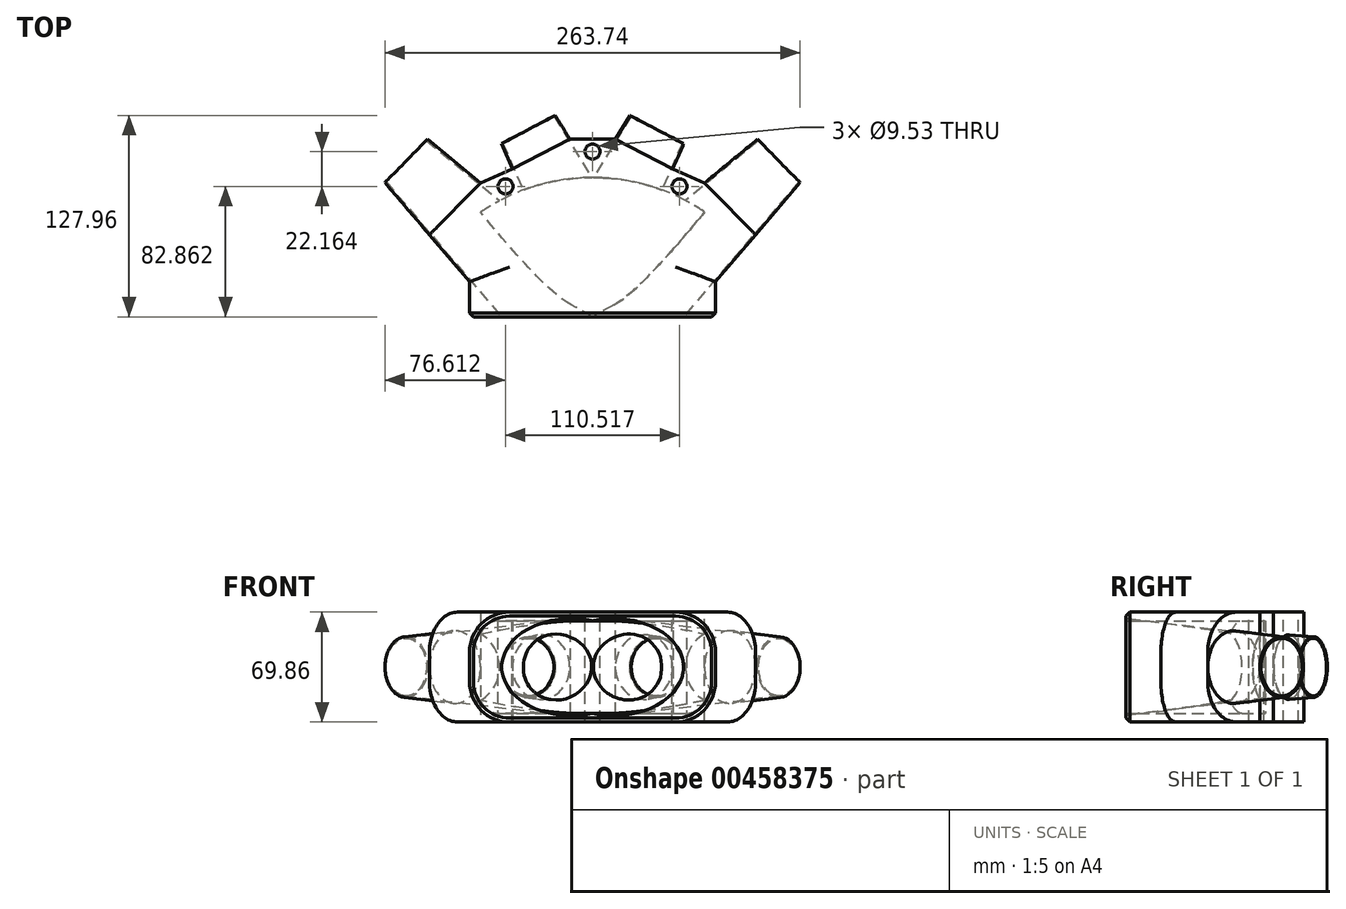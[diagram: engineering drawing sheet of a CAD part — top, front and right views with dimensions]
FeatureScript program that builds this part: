
annotation { "Feature Type Name" : "Feature", "Feature Type Description" : "" }
export const myFeature = defineFeature(function(context is Context, id is Id, definition is map)
    precondition{}
    {
        {
            var Q0;
            Q0=qCreatedBy(makeId("Top.planeOp"),FACE);
            var sketch = newSketch(context, id + "F0", { "sketchPlane" : qUnion([Q0])});
            skLineSegment(sketch, "E0", {"start": v(78.1, 11.18) * mm, "end": v(131.87, 74.09) * mm});
            skLineSegment(sketch, "E1", {"start": v(131.87, 74.09) * mm, "end": v(101.6, 11.18) * mm});
            skLineSegment(sketch, "E2", {"start": v(-5.07, 11.18) * mm, "end": v(104.82, 101.64) * mm});
            skLineSegment(sketch, "E3", {"start": v(104.82, 101.64) * mm, "end": v(101.6, 11.18) * mm});
            skLineSegment(sketch, "E4", {"start": v(19.9, 11.18) * mm, "end": v(57.9, 98.84) * mm});
            skLineSegment(sketch, "E5", {"start": v(57.9, 98.84) * mm, "end": v(101.6, 11.18) * mm});
            skLineSegment(sketch, "E6", {"start": v(-42.1, 11.18) * mm, "end": v(23.72, 116.78) * mm});
            skLineSegment(sketch, "E7", {"start": v(23.72, 116.78) * mm, "end": v(101.6, 11.18) * mm});
            skLineSegment(sketch, "E8", {"start": v(23.72, 116.78) * mm, "end": v(57.9, 98.84) * mm});
            skLineSegment(sketch, "E9", {"start": v(104.82, 101.64) * mm, "end": v(131.87, 74.09) * mm});
            skLineSegment(sketch, "E10.MirrorCS", {"start": v(-23.72, 116.78) * mm, "end": v(-57.9, 98.84) * mm});
            skLineSegment(sketch, "E11.MirrorCS", {"start": v(-104.82, 101.64) * mm, "end": v(-131.87, 74.09) * mm});
            skLineSegment(sketch, "E12.MirrorCS", {"start": v(42.1, 11.18) * mm, "end": v(-23.72, 116.78) * mm});
            skLineSegment(sketch, "E13.MirrorCS", {"start": v(-19.9, 11.18) * mm, "end": v(-57.9, 98.84) * mm});
            skLineSegment(sketch, "E14.MirrorCS", {"start": v(5.07, 11.18) * mm, "end": v(-104.82, 101.64) * mm});
            skLineSegment(sketch, "E15.MirrorCS", {"start": v(-78.1, 11.18) * mm, "end": v(-131.87, 74.09) * mm});
            skLineSegment(sketch, "E16", {"start": v(-78.1, 11.18) * mm, "end": v(-42.1, 11.18) * mm});
            skLineSegment(sketch, "E17", {"start": v(-42.1, 11.18) * mm, "end": v(-19.9, 11.18) * mm});
            skLineSegment(sketch, "E18", {"start": v(-19.9, 11.18) * mm, "end": v(-5.07, 11.18) * mm});
            skLineSegment(sketch, "E19", {"start": v(-5.07, 11.18) * mm, "end": v(5.07, 11.18) * mm});
            skLineSegment(sketch, "E20", {"start": v(5.07, 11.18) * mm, "end": v(19.9, 11.18) * mm});
            skLineSegment(sketch, "E21", {"start": v(19.9, 11.18) * mm, "end": v(42.1, 11.18) * mm});
            skLineSegment(sketch, "E22", {"start": v(42.1, 11.18) * mm, "end": v(78.1, 11.18) * mm});
            skSolve(sketch);
        }
        {
            var Q0;
            Q0=sQuery(id+"F0.wireOp",EDGE,"E11.MirrorCS");
            cPlane(context, id + "F1", {"entities" : qUnion([Q0]), "cplaneType" : CPlaneType.LINE_ANGLE, "offset" : 25 * mm, "angle" : 270 * degree, "width" : 150 * mm, "height" : 150 * mm});
        }
        {
            var Q0;
            Q0=sQuery(id+"F0.wireOp",EDGE,"E10.MirrorCS");
            cPlane(context, id + "F2", {"entities" : qUnion([Q0]), "cplaneType" : CPlaneType.LINE_ANGLE, "offset" : 25 * mm, "angle" : 180 * degree, "width" : 150 * mm, "height" : 150 * mm});
        }
        {
            var Q0;
            Q0=sQuery(id+"F0.wireOp",EDGE,"E8");
            cPlane(context, id + "F3", {"entities" : qUnion([Q0]), "cplaneType" : CPlaneType.LINE_ANGLE, "offset" : 25 * mm, "angle" : 0 * degree, "width" : 150 * mm, "height" : 150 * mm});
        }
        {
            var Q0;
            Q0=sQuery(id+"F0.wireOp",EDGE,"E9");
            cPlane(context, id + "F4", {"entities" : qUnion([Q0]), "cplaneType" : CPlaneType.LINE_ANGLE, "offset" : 25 * mm, "angle" : 90 * degree, "width" : 150 * mm, "height" : 150 * mm});
        }
        {
            var Q0;
            Q0=qCreatedBy(id+"F1.planeOp",FACE);
            var sketch = newSketch(context, id + "F5", { "sketchPlane" : qUnion([Q0])});
            skCircle(sketch, "E23", {"center": v(20.21, 0) * mm, "radius": 19.3 * mm});
            skCircle(sketch, "E24", {"center": v(20.21, 0) * mm, "radius": 18.35 * mm});
            skSolve(sketch);
        }
        {
            var Q0;
            Q0=qCreatedBy(id+"F2.planeOp",FACE);
            var sketch = newSketch(context, id + "F6", { "sketchPlane" : qUnion([Q0])});
            skCircle(sketch, "E25", {"center": v(-13.96, 0) * mm, "radius": 19.3 * mm});
            skCircle(sketch, "E26", {"center": v(-13.96, 0) * mm, "radius": 18.35 * mm});
            skSolve(sketch);
        }
        {
            var Q0;
            Q0=qCreatedBy(id+"F3.planeOp",FACE);
            var sketch = newSketch(context, id + "F7", { "sketchPlane" : qUnion([Q0])});
            skCircle(sketch, "E27", {"center": v(13.96, 0) * mm, "radius": 19.3 * mm});
            skCircle(sketch, "E28", {"center": v(13.96, 0) * mm, "radius": 18.35 * mm});
            skSolve(sketch);
        }
        {
            var Q0;
            Q0=qCreatedBy(id+"F4.planeOp",FACE);
            var sketch = newSketch(context, id + "F8", { "sketchPlane" : qUnion([Q0])});
            skCircle(sketch, "E29", {"center": v(-20.21, 0) * mm, "radius": 19.3 * mm});
            skCircle(sketch, "E30", {"center": v(-20.21, 0) * mm, "radius": 18.35 * mm});
            skSolve(sketch);
        }
        {
            var Q0;
            Q0=qCreatedBy(makeId("Top.planeOp"),FACE);
            var sketch = newSketch(context, id + "F9", { "sketchPlane" : qUnion([Q0])});
            skLineSegment(sketch, "E31", {"start": v(-78.1, 11.18) * mm, "end": v(78.1, 11.18) * mm});
            skLineSegment(sketch, "E32.bottom", {"start": v(-78.1, 11.18) * mm, "end": v(101.6, 11.18) * mm});
            skLineSegment(sketch, "E32.top", {"start": v(-78.1, -11.18) * mm, "end": v(78.1, -11.18) * mm});
            skLineSegment(sketch, "E32.left", {"start": v(-78.1, 11.18) * mm, "end": v(-78.1, -11.18) * mm});
            skLineSegment(sketch, "E32.right", {"start": v(78.1, 11.18) * mm, "end": v(78.1, -11.18) * mm});
            skCircle(sketch, "E33", {"center": v(-55.26, 71.68) * mm, "radius": 8.37 * mm});
            skCircle(sketch, "E34", {"center": v(0, 93.85) * mm, "radius": 8 * mm});
            skCircle(sketch, "E35", {"center": v(55.26, 71.68) * mm, "radius": 8.37 * mm});
            skLineSegment(sketch, "E36", {"start": v(-14.41, 101.85) * mm, "end": v(14.41, 101.85) * mm});
            skLineSegment(sketch, "E37", {"start": v(-71.15, 73.92) * mm, "end": v(-50.9, 82.7) * mm});
            skLineSegment(sketch, "E38", {"start": v(50.9, 82.7) * mm, "end": v(71.15, 73.92) * mm});
            skLineSegment(sketch, "E39", {"start": v(-78.1, 11.18) * mm, "end": v(-59, -11.18) * mm});
            skLineSegment(sketch, "E40", {"start": v(78.1, 11.18) * mm, "end": v(59, -11.18) * mm});
            skLineSegment(sketch, "E41", {"start": v(-50.9, 82.7) * mm, "end": v(-57.9, 98.84) * mm});
            skLineSegment(sketch, "E42", {"start": v(-57.9, 98.84) * mm, "end": v(-23.72, 116.78) * mm});
            skLineSegment(sketch, "E43", {"start": v(-23.72, 116.78) * mm, "end": v(-14.41, 101.85) * mm});
            skLineSegment(sketch, "E44", {"start": v(14.41, 101.85) * mm, "end": v(23.72, 116.78) * mm});
            skLineSegment(sketch, "E45", {"start": v(23.72, 116.78) * mm, "end": v(57.9, 98.84) * mm});
            skLineSegment(sketch, "E46", {"start": v(57.9, 98.84) * mm, "end": v(50.9, 82.7) * mm});
            skLineSegment(sketch, "E47", {"start": v(71.15, 73.92) * mm, "end": v(104.82, 101.64) * mm});
            skLineSegment(sketch, "E48", {"start": v(104.82, 101.64) * mm, "end": v(131.87, 74.09) * mm});
            skLineSegment(sketch, "E49", {"start": v(131.87, 74.09) * mm, "end": v(78.1, 11.18) * mm});
            skLineSegment(sketch, "E50", {"start": v(-71.15, 73.92) * mm, "end": v(-104.82, 101.64) * mm});
            skLineSegment(sketch, "E51", {"start": v(-104.82, 101.64) * mm, "end": v(-131.87, 74.09) * mm});
            skLineSegment(sketch, "E52", {"start": v(-131.87, 74.09) * mm, "end": v(-78.1, 11.18) * mm});
            skSolve(sketch);
        }
        {
            var Q0;
            Q0=makeQuery(id+"F9.imprint","IMPRINT",FACE,{"disambiguationData":[TD([[makeQuery(id+"F9.imprint","IMPRINT",EDGE,{"derivedFrom":sQuery(id+"F9.wireOp",EDGE,"E33")}),1.0]])]});
            var Q1;
            Q1=makeQuery(id+"F9.imprint","IMPRINT",FACE,{"disambiguationData":[TD([[makeQuery(id+"F9.imprint","IMPRINT",EDGE,{"derivedFrom":sQuery(id+"F9.wireOp",EDGE,"E34")}),1.0]])]});
            var Q2;
            Q2=makeQuery(id+"F9.imprint","IMPRINT",FACE,{"disambiguationData":[TD([[makeQuery(id+"F9.imprint","IMPRINT",EDGE,{"derivedFrom":sQuery(id+"F9.wireOp",EDGE,"E35")}),1.0]])]});
            var Q3;
            {var subQ0=sQuery(id+"F9.wireOp",EDGE,"E39");Q3=makeQuery(id+"F9.imprint","IMPRINT",FACE,{"disambiguationData":[TD([[makeQuery(id+"F9.imprint","IMPRINT",EDGE,{"derivedFrom":subQ0}),1.0]])]});}
            var Q4;
            {var subQ7=sQuery(id+"F9.wireOp",EDGE,"E33");Q4=makeQuery(id+"F9.imprint","IMPRINT",FACE,{"disambiguationData":[TD([[makeQuery(id+"F9.imprint","IMPRINT",EDGE,{"derivedFrom":subQ7}),-1.0]])]});}
            var Q5;
            {var subQ0=sQuery(id+"F9.wireOp",EDGE,"E32.left");Q5=makeQuery(id+"F9.imprint","IMPRINT",FACE,{"disambiguationData":[TD([[makeQuery(id+"F9.imprint","IMPRINT",EDGE,{"derivedFrom":subQ0}),1.0]])]});}
            var Q6;
            {var subQ0=sQuery(id+"F9.wireOp",EDGE,"E32.right");Q6=makeQuery(id+"F9.imprint","IMPRINT",FACE,{"disambiguationData":[TD([[makeQuery(id+"F9.imprint","IMPRINT",EDGE,{"derivedFrom":subQ0}),-1.0]])]});}
            extrude(context, id + "F10", {"entities" : qUnion([Q0, Q1, Q2, Q3, Q4, Q5, Q6]), "endBound" : BoundingType.SYMMETRIC, "depth" : 69.85 * mm});
        }
        {
            var Q0;
            Q0=qCreatedBy(makeId("Top.planeOp"),FACE);
            var sketch = newSketch(context, id + "F11", { "sketchPlane" : qUnion([Q0])});
            skLineSegment(sketch, "E53", {"start": v(118.35, 87.86) * mm, "end": v(0, -28.32) * mm});
            skLineSegment(sketch, "E54", {"start": v(0, -28.32) * mm, "end": v(-118.35, 87.86) * mm});
            skSolve(sketch);
        }
        {
            var Q0;
            Q0=makeQuery(id+"F10.opExtrude","SWEPT_FACE",FACE,{"disambiguationData":[OSD([sQuery(id+"F9.wireOp",EDGE,"E51")])]});
            var Q1;
            Q1=makeQuery(id+"F10.opExtrude","CAP_VERTEX",VERTEX,{"disambiguationData":[OSD([sQuery(id+"F9.wireOp",EDGE,"E37"),sQuery(id+"F9.wireOp",EDGE,"E50")])],"isStart":true});
            extrude(context, id + "F12", {"entities" : qUnion([Q0]), "operationType" : NewBodyOperationType.REMOVE, "endBound" : BoundingType.UP_TO_VERTEX, "oppositeDirection" : true, "endBoundEntityVertex" : qUnion([Q1]), "depth" : 25 * mm, "hasDraft" : true, "draftAngle" : 5 * degree});
        }
        {
            var Q0;
            Q0=makeQuery(id+"F10.opExtrude","SWEPT_FACE",FACE,{"disambiguationData":[OSD([sQuery(id+"F9.wireOp",EDGE,"E42")])]});
            var Q1;
            Q1=makeQuery(id+"F10.opExtrude","CAP_VERTEX",VERTEX,{"disambiguationData":[OSD([sQuery(id+"F9.wireOp",EDGE,"E36"),sQuery(id+"F9.wireOp",EDGE,"E43")])],"isStart":false});
            extrude(context, id + "F13", {"entities" : qUnion([Q0]), "operationType" : NewBodyOperationType.REMOVE, "endBound" : BoundingType.UP_TO_VERTEX, "oppositeDirection" : true, "endBoundEntityVertex" : qUnion([Q1]), "depth" : 25 * mm, "hasDraft" : true, "draftAngle" : 5 * degree});
        }
        {
            var Q0;
            Q0=makeQuery(id+"F10.opExtrude","SWEPT_FACE",FACE,{"disambiguationData":[OSD([sQuery(id+"F9.wireOp",EDGE,"E45")])]});
            var Q1;
            Q1=makeQuery(id+"F10.opExtrude","CAP_VERTEX",VERTEX,{"disambiguationData":[OSD([sQuery(id+"F9.wireOp",EDGE,"E36"),sQuery(id+"F9.wireOp",EDGE,"E44")])],"isStart":false});
            extrude(context, id + "F14", {"entities" : qUnion([Q0]), "operationType" : NewBodyOperationType.REMOVE, "endBound" : BoundingType.UP_TO_VERTEX, "oppositeDirection" : true, "endBoundEntityVertex" : qUnion([Q1]), "depth" : 25 * mm, "hasDraft" : true, "draftAngle" : 5 * degree});
        }
        {
            var Q0;
            Q0=makeQuery(id+"F10.opExtrude","SWEPT_FACE",FACE,{"disambiguationData":[OSD([sQuery(id+"F9.wireOp",EDGE,"E48")])]});
            var Q1;
            Q1=makeQuery(id+"F10.opExtrude","CAP_VERTEX",VERTEX,{"disambiguationData":[OSD([sQuery(id+"F9.wireOp",EDGE,"E38"),sQuery(id+"F9.wireOp",EDGE,"E47")])],"isStart":false});
            extrude(context, id + "F15", {"entities" : qUnion([Q0]), "operationType" : NewBodyOperationType.REMOVE, "endBound" : BoundingType.UP_TO_VERTEX, "oppositeDirection" : true, "endBoundEntityVertex" : qUnion([Q1]), "depth" : 25 * mm, "hasDraft" : true, "draftAngle" : 5 * degree});
        }
        {
            var Q0;
            Q0=makeQuery(id+"F6.imprint","IMPRINT",FACE,{"disambiguationData":[TD([[makeQuery(id+"F6.imprint","IMPRINT",EDGE,{"derivedFrom":sQuery(id+"F6.wireOp",EDGE,"E25")}),1.0]])]});
            var Q1;
            Q1=makeQuery(id+"F6.imprint","IMPRINT",FACE,{"disambiguationData":[TD([[makeQuery(id+"F6.imprint","IMPRINT",EDGE,{"derivedFrom":sQuery(id+"F6.wireOp",EDGE,"E26")}),1.0]])]});
            extrude(context, id + "F16", {"entities" : qUnion([Q0, Q1]), "operationType" : NewBodyOperationType.ADD, "endBound" : BoundingType.UP_TO_NEXT, "oppositeDirection" : true, "depth" : 25 * mm, "hasDraft" : true, "draftAngle" : 4 * degree});
        }
        {
            var Q0;
            Q0=makeQuery(id+"F7.imprint","IMPRINT",FACE,{"disambiguationData":[TD([[makeQuery(id+"F7.imprint","IMPRINT",EDGE,{"derivedFrom":sQuery(id+"F7.wireOp",EDGE,"E27")}),1.0]])]});
            var Q1;
            Q1=makeQuery(id+"F7.imprint","IMPRINT",FACE,{"disambiguationData":[TD([[makeQuery(id+"F7.imprint","IMPRINT",EDGE,{"derivedFrom":sQuery(id+"F7.wireOp",EDGE,"E28")}),1.0]])]});
            extrude(context, id + "F17", {"entities" : qUnion([Q0, Q1]), "operationType" : NewBodyOperationType.ADD, "endBound" : BoundingType.UP_TO_NEXT, "oppositeDirection" : true, "depth" : 25 * mm, "hasDraft" : true, "draftAngle" : 4 * degree});
        }
        {
            var Q0;
            Q0=makeQuery(id+"F8.imprint","IMPRINT",FACE,{"disambiguationData":[TD([[makeQuery(id+"F8.imprint","IMPRINT",EDGE,{"derivedFrom":sQuery(id+"F8.wireOp",EDGE,"E29")}),1.0]])]});
            var Q1;
            Q1=makeQuery(id+"F8.imprint","IMPRINT",FACE,{"disambiguationData":[TD([[makeQuery(id+"F8.imprint","IMPRINT",EDGE,{"derivedFrom":sQuery(id+"F8.wireOp",EDGE,"E30")}),1.0]])]});
            extrude(context, id + "F18", {"entities" : qUnion([Q0, Q1]), "operationType" : NewBodyOperationType.ADD, "endBound" : BoundingType.UP_TO_NEXT, "oppositeDirection" : true, "depth" : 25 * mm, "hasDraft" : true, "draftAngle" : 5 * degree});
        }
        {
            var Q0;
            Q0=makeQuery(id+"F5.imprint","IMPRINT",FACE,{"disambiguationData":[TD([[makeQuery(id+"F5.imprint","IMPRINT",EDGE,{"derivedFrom":sQuery(id+"F5.wireOp",EDGE,"E23")}),1.0]])]});
            var Q1;
            Q1=makeQuery(id+"F5.imprint","IMPRINT",FACE,{"disambiguationData":[TD([[makeQuery(id+"F5.imprint","IMPRINT",EDGE,{"derivedFrom":sQuery(id+"F5.wireOp",EDGE,"E24")}),1.0]])]});
            extrude(context, id + "F19", {"entities" : qUnion([Q0, Q1]), "operationType" : NewBodyOperationType.ADD, "endBound" : BoundingType.UP_TO_NEXT, "oppositeDirection" : true, "depth" : 25 * mm, "hasDraft" : true, "draftAngle" : 5 * degree});
        }
        {
            var Q0;
            Q0=makeQuery(id+"F5.imprint","IMPRINT",FACE,{"disambiguationData":[TD([[makeQuery(id+"F5.imprint","IMPRINT",EDGE,{"derivedFrom":sQuery(id+"F5.wireOp",EDGE,"E24")}),1.0]])]});
            extrude(context, id + "F20", {"entities" : qUnion([Q0]), "operationType" : NewBodyOperationType.REMOVE, "endBound" : BoundingType.THROUGH_ALL, "oppositeDirection" : true, "depth" : 25 * mm, "hasDraft" : true, "draftAngle" : 5 * degree});
        }
        {
            var Q0;
            Q0=makeQuery(id+"F6.imprint","IMPRINT",FACE,{"disambiguationData":[TD([[makeQuery(id+"F6.imprint","IMPRINT",EDGE,{"derivedFrom":sQuery(id+"F6.wireOp",EDGE,"E26")}),1.0]])]});
            extrude(context, id + "F21", {"entities" : qUnion([Q0]), "operationType" : NewBodyOperationType.REMOVE, "endBound" : BoundingType.THROUGH_ALL, "oppositeDirection" : true, "depth" : 25 * mm, "hasDraft" : true, "draftAngle" : 4 * degree});
        }
        {
            var Q0;
            Q0=makeQuery(id+"F7.imprint","IMPRINT",FACE,{"disambiguationData":[TD([[makeQuery(id+"F7.imprint","IMPRINT",EDGE,{"derivedFrom":sQuery(id+"F7.wireOp",EDGE,"E28")}),1.0]])]});
            extrude(context, id + "F22", {"entities" : qUnion([Q0]), "operationType" : NewBodyOperationType.REMOVE, "endBound" : BoundingType.THROUGH_ALL, "oppositeDirection" : true, "depth" : 25 * mm, "hasDraft" : true, "draftAngle" : 4 * degree});
        }
        {
            var Q0;
            Q0=makeQuery(id+"F8.imprint","IMPRINT",FACE,{"disambiguationData":[TD([[makeQuery(id+"F8.imprint","IMPRINT",EDGE,{"derivedFrom":sQuery(id+"F8.wireOp",EDGE,"E30")}),1.0]])]});
            extrude(context, id + "F23", {"entities" : qUnion([Q0]), "operationType" : NewBodyOperationType.REMOVE, "endBound" : BoundingType.THROUGH_ALL, "oppositeDirection" : true, "depth" : 25 * mm, "hasDraft" : true, "draftAngle" : 5 * degree});
        }
        {
            var Q0;
            Q0=sQuery(id+"F11.wireOp",EDGE,"E53");
            cPlane(context, id + "F24", {"entities" : qUnion([Q0]), "cplaneType" : CPlaneType.LINE_ANGLE, "offset" : 25 * mm, "angle" : 270 * degree, "width" : 150 * mm, "height" : 150 * mm});
        }
        {
            var Q0;
            Q0=qCreatedBy(id+"F24.planeOp",FACE);
            var sketch = newSketch(context, id + "F25", { "sketchPlane" : qUnion([Q0])});
            skLineSegment(sketch, "E55.bottom", {"start": v(19.84, 28.58) * mm, "end": v(-80.16, 28.57) * mm});
            skLineSegment(sketch, "E55.top", {"start": v(19.84, 0) * mm, "end": v(-80.16, 0) * mm});
            skLineSegment(sketch, "E55.left", {"start": v(19.84, 28.58) * mm, "end": v(19.84, 0) * mm});
            skLineSegment(sketch, "E55.right", {"start": v(-80.16, 28.57) * mm, "end": v(-80.16, 0) * mm});
            skLineSegment(sketch, "E56.MirrorCS", {"start": v(19.84, -28.57) * mm, "end": v(19.84, 0) * mm});
            skLineSegment(sketch, "E57.MirrorCS", {"start": v(19.84, -28.57) * mm, "end": v(-80.16, -28.57) * mm});
            skLineSegment(sketch, "E58.MirrorCS", {"start": v(-80.16, -28.57) * mm, "end": v(-80.16, 0) * mm});
            skSolve(sketch);
        }
        {
            var Q0;
            {var subQ0=sQuery(id+"F9.wireOp",EDGE,"E52");var subQ1=sQuery(id+"F9.wireOp",EDGE,"E39");Q0=makeQuery(id+"F9ZJCy9J1rFDsAn_1.boolean.opBoolean","SPLIT",EDGE,{"disambiguationData":[TD([makeQuery(id+"F12.boolean.opBoolean","COPY",FACE,{"derivedFrom":makeQuery(id+"F12.opExtrude","CAP_FACE",FACE,{"disambiguationData":[OSD([dummyQuery(id+"F12.vertexPlane.planeOp",FACE)])],"isStart":false})})])],"derivedFrom":makeQuery(id+"F10.opExtrude","CAP_EDGE",EDGE,{"disambiguationData":[OSD([subQ1,subQ0])],"isStart":false})});}
            var Q1;
            {var subQ0=sQuery(id+"F9.wireOp",EDGE,"E52");var subQ1=sQuery(id+"F9.wireOp",EDGE,"E39");Q1=makeQuery(id+"F9ZJCy9J1rFDsAn_1.boolean.opBoolean","SPLIT",EDGE,{"disambiguationData":[TD([makeQuery(id+"F12.boolean.opBoolean","COPY",FACE,{"derivedFrom":makeQuery(id+"F12.opExtrude","CAP_FACE",FACE,{"disambiguationData":[OSD([dummyQuery(id+"F12.vertexPlane.planeOp",FACE)])],"isStart":false})})])],"derivedFrom":makeQuery(id+"F10.opExtrude","CAP_EDGE",EDGE,{"disambiguationData":[OSD([subQ1,subQ0])],"isStart":true})});}
            var Q2;
            {var subQ0=sQuery(id+"F9.wireOp",EDGE,"E32.top");var subQ1=sQuery(id+"F9.wireOp",EDGE,"E52");var subQ2=sQuery(id+"F9.wireOp",EDGE,"E39");Q2=makeQuery(id+"F9ZJCy9J1rFDsAn_1.boolean.opBoolean","SPLIT",EDGE,{"disambiguationData":[TD([makeQuery(id+"F10.opExtrude","SWEPT_FACE",FACE,{"disambiguationData":[OSD([subQ0])]})])],"derivedFrom":makeQuery(id+"F10.opExtrude","CAP_EDGE",EDGE,{"disambiguationData":[OSD([subQ2,subQ1])],"isStart":false})});}
            var Q3;
            {var subQ0=sQuery(id+"F9.wireOp",EDGE,"E32.top");var subQ1=sQuery(id+"F9.wireOp",EDGE,"E52");var subQ2=sQuery(id+"F9.wireOp",EDGE,"E39");Q3=makeQuery(id+"F9ZJCy9J1rFDsAn_1.boolean.opBoolean","SPLIT",EDGE,{"disambiguationData":[TD([makeQuery(id+"F10.opExtrude","SWEPT_FACE",FACE,{"disambiguationData":[OSD([subQ0])]})])],"derivedFrom":makeQuery(id+"F10.opExtrude","CAP_EDGE",EDGE,{"disambiguationData":[OSD([subQ2,subQ1])],"isStart":true})});}
            var Q4;
            {var subQ0=sQuery(id+"F9.wireOp",EDGE,"E49");var subQ1=sQuery(id+"F9.wireOp",EDGE,"E40");Q4=makeQuery(id+"F9ZJCy9J1rFDsAn_1.boolean.opBoolean","SPLIT",EDGE,{"disambiguationData":[TD([makeQuery(id+"F15.boolean.opBoolean","COPY",FACE,{"derivedFrom":makeQuery(id+"F15.opExtrude","CAP_FACE",FACE,{"disambiguationData":[OSD([dummyQuery(id+"F15.vertexPlane.planeOp",FACE)])],"isStart":false})})])],"derivedFrom":makeQuery(id+"F10.opExtrude","CAP_EDGE",EDGE,{"disambiguationData":[OSD([subQ1,subQ0])],"isStart":false})});}
            var Q5;
            {var subQ0=sQuery(id+"F9.wireOp",EDGE,"E32.top");var subQ1=sQuery(id+"F9.wireOp",EDGE,"E49");var subQ2=sQuery(id+"F9.wireOp",EDGE,"E40");Q5=makeQuery(id+"F9ZJCy9J1rFDsAn_1.boolean.opBoolean","SPLIT",EDGE,{"disambiguationData":[TD([makeQuery(id+"F10.opExtrude","SWEPT_FACE",FACE,{"disambiguationData":[OSD([subQ0])]})])],"derivedFrom":makeQuery(id+"F10.opExtrude","CAP_EDGE",EDGE,{"disambiguationData":[OSD([subQ2,subQ1])],"isStart":false})});}
            var Q6;
            {var subQ0=sQuery(id+"F9.wireOp",EDGE,"E49");var subQ1=sQuery(id+"F9.wireOp",EDGE,"E40");Q6=makeQuery(id+"F9ZJCy9J1rFDsAn_1.boolean.opBoolean","SPLIT",EDGE,{"disambiguationData":[TD([makeQuery(id+"F15.boolean.opBoolean","COPY",FACE,{"derivedFrom":makeQuery(id+"F15.opExtrude","CAP_FACE",FACE,{"disambiguationData":[OSD([dummyQuery(id+"F15.vertexPlane.planeOp",FACE)])],"isStart":false})})])],"derivedFrom":makeQuery(id+"F10.opExtrude","CAP_EDGE",EDGE,{"disambiguationData":[OSD([subQ1,subQ0])],"isStart":true})});}
            fillet(context, id + "F26", {"entities" : qUnion([Q0, Q1, Q2, Q3, Q4, Q5, Q6]), "radius" : 25.4 * mm, "tangentPropagation" : true, "allowEdgeOverflow" : false});
        }
        {
            var Q0;
            Q0=makeQuery(id+"F10.opExtrude","CAP_FACE",FACE,{"disambiguationData":[OSD([sQuery(id+"F9.wireOp",EDGE,"E32.top"),sQuery(id+"F9.wireOp",EDGE,"E36"),sQuery(id+"F9.wireOp",EDGE,"E37"),sQuery(id+"F9.wireOp",EDGE,"E38"),sQuery(id+"F9.wireOp",EDGE,"E39"),sQuery(id+"F9.wireOp",EDGE,"E40"),sQuery(id+"F9.wireOp",EDGE,"E41"),sQuery(id+"F9.wireOp",EDGE,"E42"),sQuery(id+"F9.wireOp",EDGE,"E43"),sQuery(id+"F9.wireOp",EDGE,"E44"),sQuery(id+"F9.wireOp",EDGE,"E45"),sQuery(id+"F9.wireOp",EDGE,"E46"),sQuery(id+"F9.wireOp",EDGE,"E47"),sQuery(id+"F9.wireOp",EDGE,"E48"),sQuery(id+"F9.wireOp",EDGE,"E49"),sQuery(id+"F9.wireOp",EDGE,"E50"),sQuery(id+"F9.wireOp",EDGE,"E51"),sQuery(id+"F9.wireOp",EDGE,"E52")])],"isStart":false});
            var sketch = newSketch(context, id + "F27", { "sketchPlane" : qUnion([Q0])});
            skCircle(sketch, "E59", {"center": v(0, 93.85) * mm, "radius": 4.76 * mm});
            skCircle(sketch, "E60", {"center": v(-55.26, 71.68) * mm, "radius": 4.76 * mm});
            skCircle(sketch, "E61", {"center": v(55.26, 71.68) * mm, "radius": 4.76 * mm});
            skSolve(sketch);
        }
        {
            var Q0;
            Q0=qSketchRegion(id+"F27",true);
            extrude(context, id + "F28", {"entities" : qUnion([Q0]), "operationType" : NewBodyOperationType.REMOVE, "endBound" : BoundingType.THROUGH_ALL, "oppositeDirection" : true, "depth" : 25 * mm});
        }
        {
            var Q0;
            Q0=qCreatedBy(makeId("Right.planeOp"),FACE);
            var sketch = newSketch(context, id + "F29", { "sketchPlane" : qUnion([Q0])});
            skLineSegment(sketch, "E62", {"start": v(-49.28, 0) * mm, "end": v(-49.28, 31.18) * mm});
            skLineSegment(sketch, "E63", {"start": v(-49.28, 31.18) * mm, "end": v(-49.28, -28.68) * mm});
            skSolve(sketch);
        }
        {
            var Q0;
            Q0=qCreatedBy(makeId("Right.planeOp"),FACE);
            var sketch = newSketch(context, id + "F30", { "sketchPlane" : qUnion([Q0])});
            skLineSegment(sketch, "E64.bottom", {"start": v(-28.32, -29.36) * mm, "end": v(77.34, -29.36) * mm});
            skLineSegment(sketch, "E64.top", {"start": v(-28.32, 29.36) * mm, "end": v(77.34, 29.36) * mm});
            skLineSegment(sketch, "E64.left", {"start": v(-28.32, -29.36) * mm, "end": v(-28.32, 29.36) * mm});
            skLineSegment(sketch, "E64.right", {"start": v(77.34, -29.36) * mm, "end": v(77.34, 29.36) * mm});
            skSolve(sketch);
        }
        {
            var Q0;
            Q0 = qSketchRegion(id + "F30", true);
            var Q1;
            Q1=sQuery(id+"F29.wireOp",EDGE,"E63");
            revolve(context, id + "F31", {"operationType" : NewBodyOperationType.REMOVE, "entities" : qUnion([Q0]), "axis" : qUnion([Q1]), "revolveType" : RevolveType.SYMMETRIC, "oppositeDirection" : true, "angle" : 70 * degree});
        }
        {
            var Q0;
            Q0=makeQuery(id+"F31.boolean.opBoolean","COPY",EDGE,{"derivedFrom":makeQuery(id+"F31.opRevolve","CAP_EDGE",EDGE,{"disambiguationData":[OSD([sQuery(id+"F30.wireOp",EDGE,"E64.bottom")])],"isStart":true})});
            var Q1;
            Q1=makeQuery(id+"F31.boolean.opBoolean","COPY",EDGE,{"derivedFrom":makeQuery(id+"F31.opRevolve","CAP_EDGE",EDGE,{"disambiguationData":[OSD([sQuery(id+"F30.wireOp",EDGE,"E64.top")])],"isStart":true})});
            var Q2;
            Q2=makeQuery(id+"F31.boolean.opBoolean","COPY",EDGE,{"derivedFrom":makeQuery(id+"F31.opRevolve","CAP_EDGE",EDGE,{"disambiguationData":[OSD([sQuery(id+"F30.wireOp",EDGE,"E64.bottom")])],"isStart":false})});
            var Q3;
            Q3=makeQuery(id+"F31.boolean.opBoolean","COPY",EDGE,{"derivedFrom":makeQuery(id+"F31.opRevolve","CAP_EDGE",EDGE,{"disambiguationData":[OSD([sQuery(id+"F30.wireOp",EDGE,"E64.top")])],"isStart":false})});
            fillet(context, id + "F32", {"entities" : qUnion([Q0, Q1, Q2, Q3]), "radius" : 15.24 * mm, "tangentPropagation" : true, "allowEdgeOverflow" : false});
        }
        {
            var Q0;
            Q0=makeQuery(id+"F10.opExtrude","CAP_EDGE",EDGE,{"disambiguationData":[OSD([sQuery(id+"F9.wireOp",EDGE,"E32.left")])],"isStart":false});
            var Q1;
            Q1=makeQuery(id+"F10.opExtrude","CAP_EDGE",EDGE,{"disambiguationData":[OSD([sQuery(id+"F9.wireOp",EDGE,"E32.right")])],"isStart":false});
            var Q2;
            Q2=makeQuery(id+"F10.opExtrude","CAP_EDGE",EDGE,{"disambiguationData":[OSD([sQuery(id+"F9.wireOp",EDGE,"E32.right")])],"isStart":true});
            var Q3;
            Q3=makeQuery(id+"F10.opExtrude","CAP_EDGE",EDGE,{"disambiguationData":[OSD([sQuery(id+"F9.wireOp",EDGE,"E32.left")])],"isStart":true});
            fillet(context, id + "F33", {"entities" : qUnion([Q0, Q1, Q2, Q3]), "radius" : 25.4 * mm, "tangentPropagation" : true, "allowEdgeOverflow" : false});
        }
        {
            var Q0;
            Q0=makeQuery(id+"F10.opExtrude","SWEPT_EDGE",EDGE,{"disambiguationData":[OSD([sQuery(id+"F9.wireOp",EDGE,"E32.top"),sQuery(id+"F9.wireOp",EDGE,"E32.left")])]});
            chamfer(context, id + "F34", {"entities" : qUnion([Q0]), "width" : 2.54 * mm, "tangentPropagation" : true});
        }
    });
